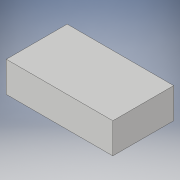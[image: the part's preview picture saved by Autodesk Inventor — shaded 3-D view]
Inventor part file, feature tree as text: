
AUTODESK INVENTOR PART (.ipt)
format: ipt  version: 2019.4 (Build 234330000, 330)  size: 87,040 bytes
history: native  units: in
note: dims shown in document units (in); Inventor stores cm internally (conversion verified against a paired STEP export)
features: extrude x1, sketch x1
ambient origin geometry x8: Origin, YZ Plane, XZ Plane, XY Plane, X Axis, Y Axis, Z Axis, Center Point
bodies: Solid1 (feature_tree)
feature tree (2):
  extrude  "Extrusion1"  Depth=0.7874in
  sketch  "Sketch1"  dims[d0=1.378in d1=0.7874in d2=0.3937in d3=0.0in]
